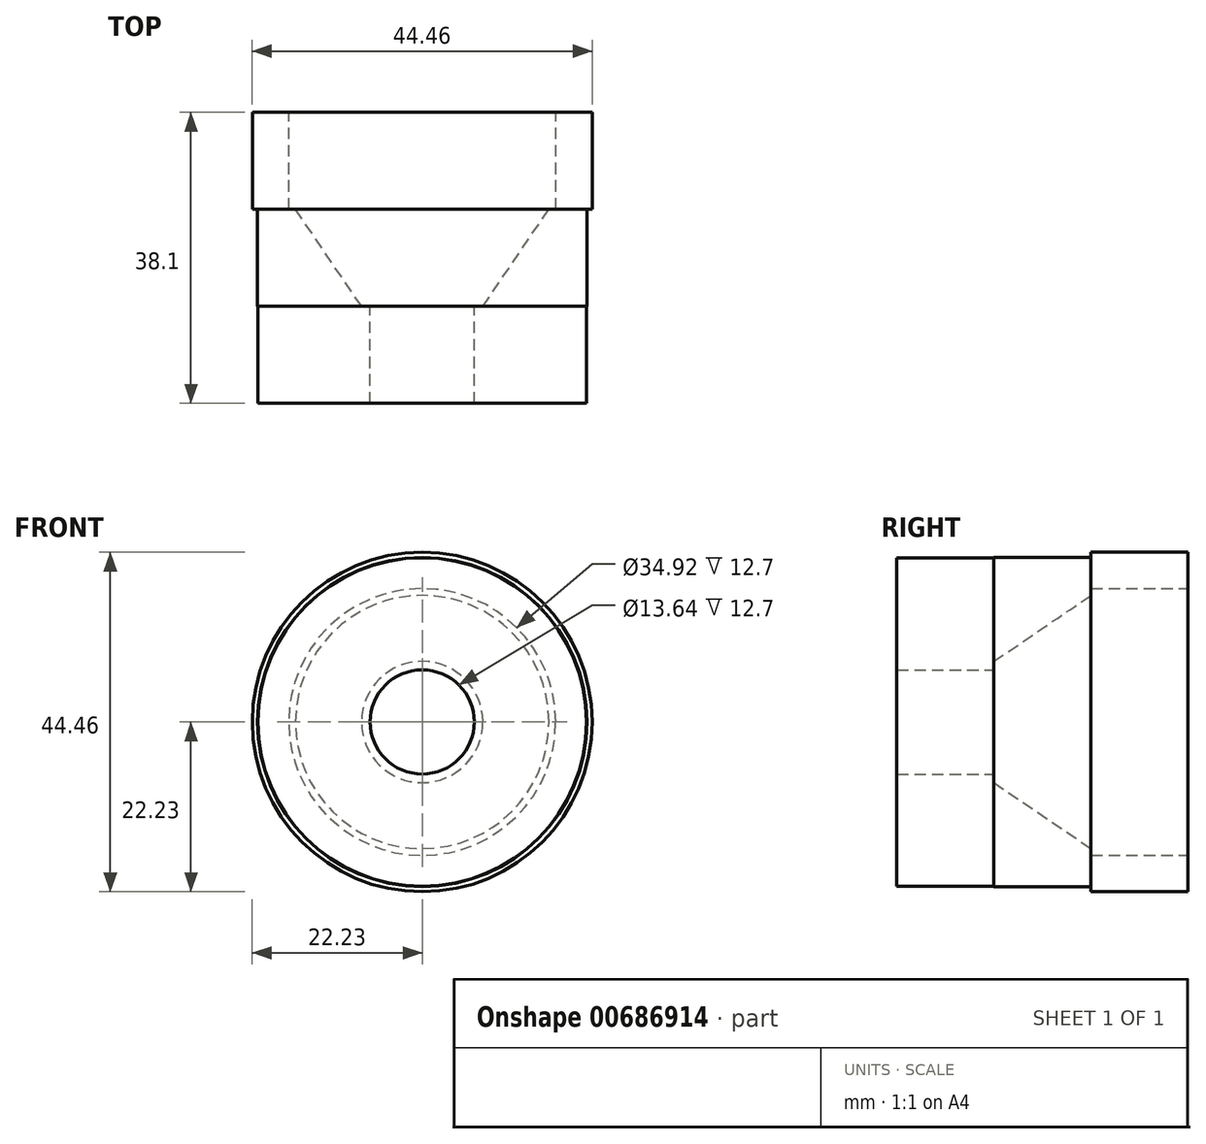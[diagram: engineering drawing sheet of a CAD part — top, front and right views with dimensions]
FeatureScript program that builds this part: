
annotation { "Feature Type Name" : "Feature", "Feature Type Description" : "" }
export const myFeature = defineFeature(function(context is Context, id is Id, definition is map)
    precondition{}
    {
        {
            var Q0;
            Q0=qCreatedBy(makeId("Front.planeOp"),FACE);
            var sketch = newSketch(context, id + "F0", { "sketchPlane" : qUnion([Q0])});
            skCircle(sketch, "E0", {"center": v(0, 0) * mm, "radius": 22.23 * mm});
            skCircle(sketch, "E1", {"center": v(0, 0) * mm, "radius": 17.46 * mm});
            skSolve(sketch);
        }
        {
            var Q0;
            Q0 = qSketchRegion(id + "F0", true);
            extrude(context, id + "F1", {"entities" : qUnion([Q0]), "depth" : 12.7 * mm, "offsetDistance" : 25.4 * mm});
        }
        {
            var Q0;
            Q0=qCreatedBy(makeId("Right.planeOp"),FACE);
            var sketch = newSketch(context, id + "F2", { "sketchPlane" : qUnion([Q0])});
            skLineSegment(sketch, "E2", {"start": v(-12.7, 16.58) * mm, "end": v(-25.4, 7.94) * mm});
            skLineSegment(sketch, "E3", {"start": v(-25.4, 7.94) * mm, "end": v(-25.4, 21.54) * mm});
            skLineSegment(sketch, "E4", {"start": v(-25.4, 21.54) * mm, "end": v(-12.7, 21.54) * mm});
            skLineSegment(sketch, "E5", {"start": v(-12.7, 21.54) * mm, "end": v(-12.7, 16.58) * mm});
            skSolve(sketch);
        }
        {
            var Q0;
            Q0 = qSketchRegion(id + "F2", true);
            var Q1;
            Q1=makeQuery(id+"F1.opExtrude","CAP_EDGE",EDGE,{"disambiguationData":[OSD([sQuery(id+"F0.wireOp",EDGE,"E1")])],"isStart":false});
            revolve(context, id + "F3", {"operationType" : NewBodyOperationType.ADD, "entities" : qUnion([Q0]), "axis" : qUnion([Q1]), "revolveType" : RevolveType.FULL});
        }
        {
            var Q0;
            Q0=makeQuery(id+"F3.opRevolve","SWEPT_FACE",FACE,{"disambiguationData":[OSD([sQuery(id+"F2.wireOp",EDGE,"E3")])]});
            var sketch = newSketch(context, id + "F4", { "sketchPlane" : qUnion([Q0])});
            skCircle(sketch, "E6", {"center": v(0, 0) * mm, "radius": 21.5 * mm});
            skCircle(sketch, "E7", {"center": v(0, 0) * mm, "radius": 6.82 * mm});
            skSolve(sketch);
        }
        {
            var Q0;
            Q0 = qSketchRegion(id + "F4", true);
            extrude(context, id + "F5", {"entities" : qUnion([Q0]), "operationType" : NewBodyOperationType.ADD, "depth" : 12.7 * mm, "offsetDistance" : 25.4 * mm});
        }
    });
